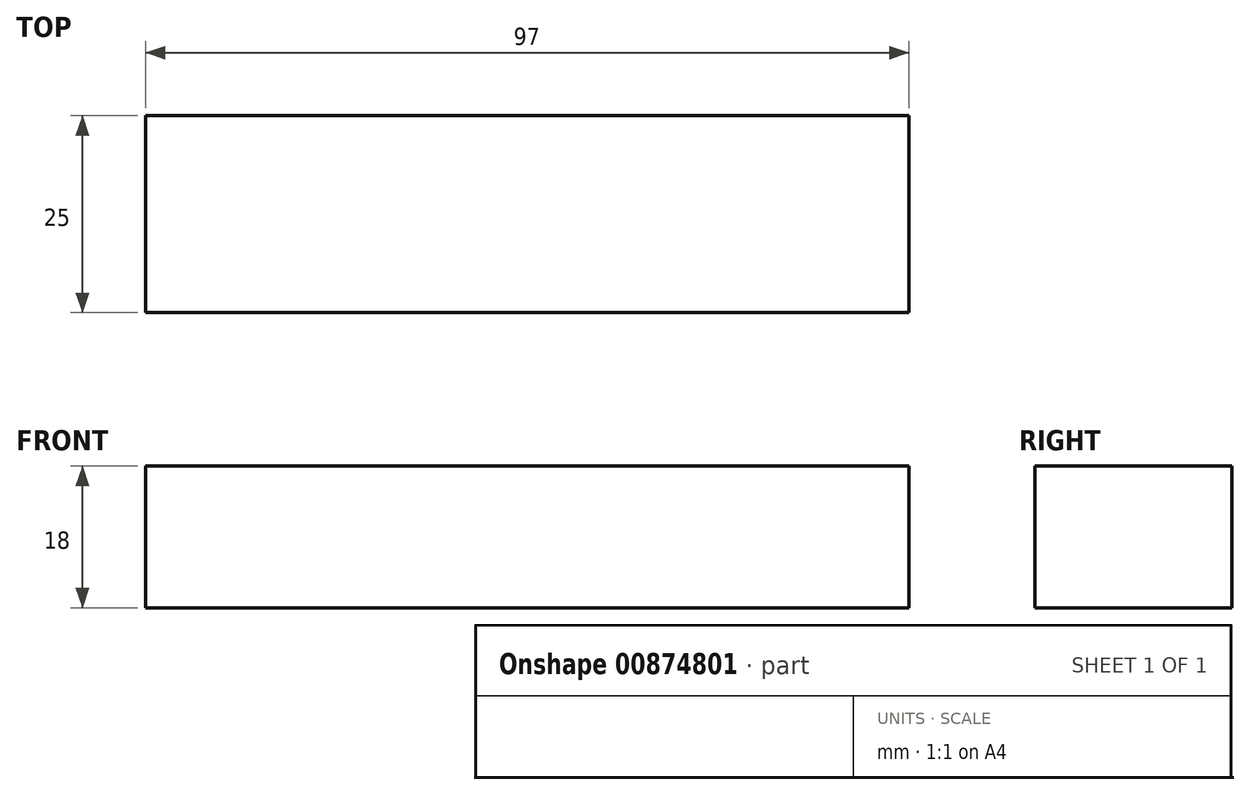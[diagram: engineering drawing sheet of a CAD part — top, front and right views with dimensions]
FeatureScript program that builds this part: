
annotation { "Feature Type Name" : "Feature", "Feature Type Description" : "" }
export const myFeature = defineFeature(function(context is Context, id is Id, definition is map)
    precondition{}
    {
        {
            var Q0;
            Q0=qCreatedBy(makeId("Front.planeOp"),FACE);
            var sketch = newSketch(context, id + "F0", { "sketchPlane" : qUnion([Q0])});
            skLineSegment(sketch, "E0.bottom", {"start": v(-22.1, 18) * mm, "end": v(74.9, 18) * mm});
            skLineSegment(sketch, "E0.top", {"start": v(-22.1, 0) * mm, "end": v(74.9, 0) * mm});
            skLineSegment(sketch, "E0.left", {"start": v(-22.1, 18) * mm, "end": v(-22.1, 0) * mm});
            skLineSegment(sketch, "E0.right", {"start": v(74.9, 18) * mm, "end": v(74.9, 0) * mm});
            skSolve(sketch);
        }
        {
            var Q0;
            Q0 = qSketchRegion(id + "F0", true);
            extrude(context, id + "F1", {"entities" : qUnion([Q0]), "depth" : 25 * mm, "offsetDistance" : 25 * mm});
        }
    });
